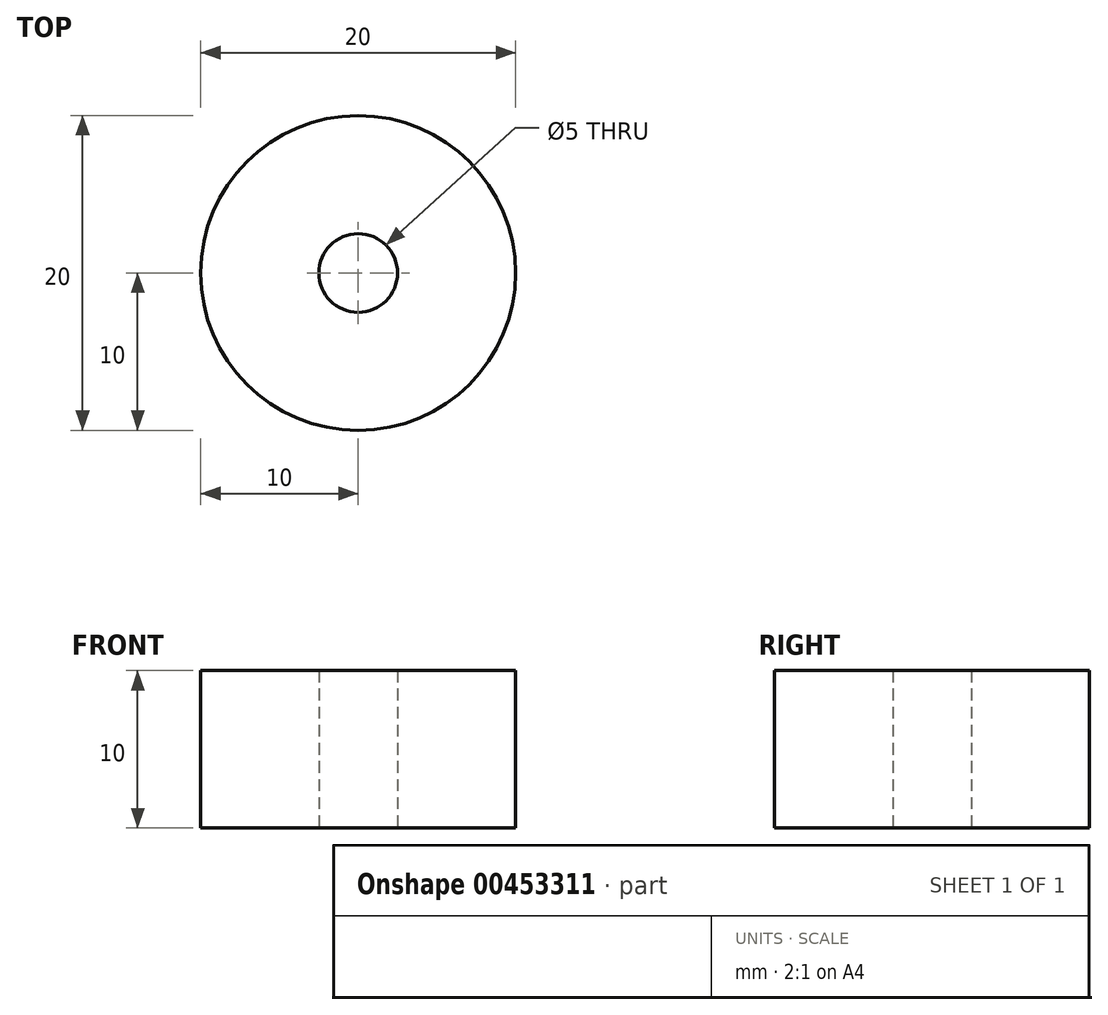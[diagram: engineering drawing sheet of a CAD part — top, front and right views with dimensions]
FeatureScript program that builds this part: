
annotation { "Feature Type Name" : "Feature", "Feature Type Description" : "" }
export const myFeature = defineFeature(function(context is Context, id is Id, definition is map)
    precondition{}
    {
        {
            var Q0;
            Q0=qCreatedBy(makeId("Top.planeOp"),FACE);
            var sketch = newSketch(context, id + "F0", { "sketchPlane" : qUnion([Q0])});
            skCircle(sketch, "E0", {"center": v(0, 0) * mm, "radius": 10 * mm});
            skSolve(sketch);
        }
        {
            var Q0;
            Q0 = qSketchRegion(id + "F0", true);
            extrude(context, id + "F1", {"entities" : qUnion([Q0]), "depth" : 10 * mm});
        }
        {
            var Q0;
            Q0=makeQuery(id+"F1.opExtrude","CAP_FACE",FACE,{"disambiguationData":[OSD([sQuery(id+"F0.wireOp",EDGE,"E0")])],"isStart":true});
            var sketch = newSketch(context, id + "F2", { "sketchPlane" : qUnion([Q0])});
            skCircle(sketch, "E1", {"center": v(0, 0) * mm, "radius": 2.5 * mm});
            skSolve(sketch);
        }
        {
            var Q0;
            Q0=makeQuery(id+"F2.imprint","IMPRINT",FACE,{"disambiguationData":[TD([[makeQuery(id+"F2.imprint","IMPRINT",EDGE,{"derivedFrom":sQuery(id+"F2.wireOp",EDGE,"E1")}),1.0]])]});
            var Q1;
            Q1=sQuery(id+"F2.wireOp",EDGE,"E1");
            extrude(context, id + "F3", {"entities" : qUnion([Q0]), "operationType" : NewBodyOperationType.REMOVE, "surfaceEntities" : qUnion([Q1]), "oppositeDirection" : true, "depth" : 25 * mm});
        }
    });
